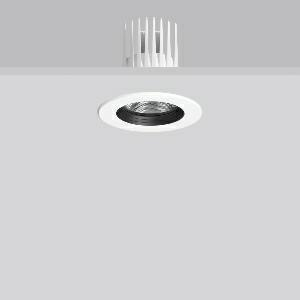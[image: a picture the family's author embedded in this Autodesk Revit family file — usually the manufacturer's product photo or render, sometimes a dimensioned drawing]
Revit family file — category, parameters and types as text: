
# Revit family: heledon_mini_e_901748_002_76_4b8c
name_source: partatom
category: Lighting Fixtures
units: mm (PartAtom-declared; Revit-internal decimal feet)

## family parameters
Cut with Voids When Loaded = No
Host = Face
Light Source = No
Part Type = Normal
Room Calculation Point = No
Round Connector Dimension = Use Diameter
Shared = No

## types (1)
- HELEDON mini E (1 x LED Modul 930, 3550 lm, 3000)
    Apparent Load = 29 VA
    Approval mark = CE
    CIE Flux Codes = 100 100 100 100 100
    Color Rendering = 90
    Color Temperature = 3000
    Default Elevation = 1800 mm
    Description = Series: HELEDON mini
Round recessed downlight. Housing: die-cast aluminium, powder-coated. Black plastic ring and recessed LED to prevent glare from the side. Optical assembly with reflector made of MIRO-Silver with 98% total light reflection for outstanding efficiency - can be changed without tools. Best colour rendering index Ra>90. Suitable for Recessed ceiling mounting. Installation without tools thanks to spring fastening system. Including separate LED converter with connecting cable 600 mm.High quality converter without flickering and stroboscopic effect. Through-wiring box (5 pole) available as accessory. The following accessories can be mounted without use of tools: interchangeable lenses, decorative glasses, honeycomb louvre, clear and frosted diffusers, white interchangeable plastic ring. 
Colour: traffic white, matt (RAL 9016)
Diameter: 124 mm
Height: 3 mm
Cut-out diameter: 114 mm
Recess height: 170 mm
Luminaire: recess height: 120 mm
Lamp: LED
Socket: without socket
Colour temperature: 3000K
Colour rendering index (CRI): 92
System power: 29 W
Rated luminous flux: 3550 lm
Luminous efficiency: 122 lm/W
Control gear: Converter, dimmable, DALI
Protection class: II
Type of protection: IP 20
    Height = 0 mm  [stored 0 ft]
    Lamp = 1 x LED Modul 930
    Lamp Light Flux = 3550 lm
    Lamp count = 1
    Length = 124 mm  [stored 0.406824 ft]
    Lifetime = 50000 h
    Luminous efficacy = 122 lm/W
    Manufacturer = RZB
    ModVariant = No
    Model = 901748.002.76
    Mounting Place = Ceiling
    Mounting Type = Recessed
    Number of Poles = 1
    OnlyDefault = Yes
    Power Factor = 1
    Product Name = HELEDON mini E
    Product group = Recessed downlights
    ProductGroupID = 402
    Protection Class = Protection class II
    Protection Degree = IP 20
    RLX_Detail_Level = 1
    RLX_Emergency_Light_Flux = 0 lm
    RLX_Emergency_Type = 0
    RLX_Emergency_Type_DB = No
    RlxData = <blob elided: 125229 chars, md5=ece4b178>
    Socket = socket
    Standby Power = 0 W
    System Light Flux = 3550 lm
    System Power = 29 W
    Type Comments = Product without accessories
    Type Image = 901657.002.jpg
    URL = http://relux.com
    VarID = ---
    Voltage = 230 V
    Voltage Range = 220-240 V
    Weight = 0.00 kg
    Width = 0 mm  [stored 0 ft]

note: [stored X ft] marks values corroborated as IEEE doubles in the binary element streams (Revit-internal decimal feet)

## geometry (parser evidence)
native form markers: Blend x4, Sweep x12
no freeform markers — native parametric forms only
